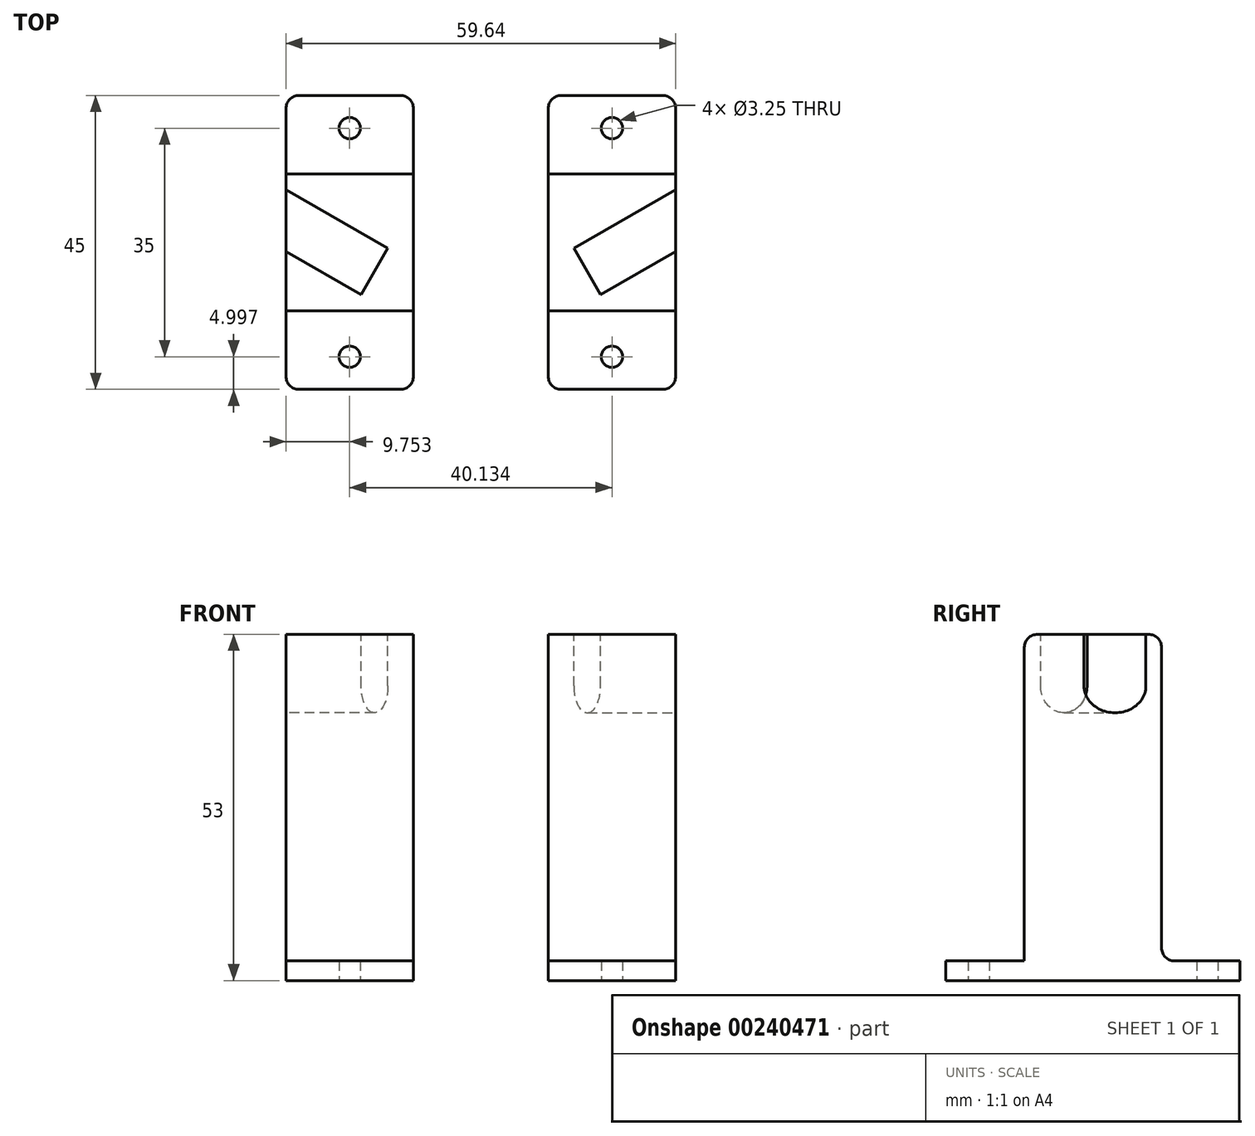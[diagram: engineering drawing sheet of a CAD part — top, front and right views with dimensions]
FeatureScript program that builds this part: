
annotation { "Feature Type Name" : "Feature", "Feature Type Description" : "" }
export const myFeature = defineFeature(function(context is Context, id is Id, definition is map)
    precondition{}
    {
        {
            var Q0;
            Q0=qCreatedBy(makeId("Top.planeOp"),FACE);
            var sketch = newSketch(context, id + "F0", { "sketchPlane" : qUnion([Q0])});
            skLineSegment(sketch, "E0.bottom", {"start": v(-29.82, 23.66) * mm, "end": v(-10.32, 23.66) * mm});
            skLineSegment(sketch, "E0.top", {"start": v(-29.82, -21.34) * mm, "end": v(-10.32, -21.34) * mm});
            skLineSegment(sketch, "E0.left", {"start": v(-29.82, 23.66) * mm, "end": v(-29.82, -21.34) * mm});
            skLineSegment(sketch, "E0.right", {"start": v(-10.32, 23.66) * mm, "end": v(-10.32, -21.34) * mm});
            skPoint(sketch, "E1", {"position": v(-20.07, 18.66) * mm});
            skPoint(sketch, "E1.positionSnap0", {"position": v(-20.07, 23.66) * mm});
            skPoint(sketch, "E2", {"position": v(-20.07, -16.34) * mm});
            skSolve(sketch);
        }
        {
            var Q0;
            Q0=makeQuery(id+"F0.imprint","IMPRINT",FACE,{"disambiguationData":[TD([[makeQuery(id+"F0.imprint","IMPRINT",EDGE,{"derivedFrom":sQuery(id+"F0.wireOp",EDGE,"E0.bottom")}),-1.0]])]});
            extrude(context, id + "F1", {"entities" : qUnion([Q0]), "depth" : 3 * mm});
        }
        {
            var Q0;
            Q0=sQuery(id+"F0.wireOp",VERTEX,"E2");
            var Q1;
            Q1=makeQuery(id+"F1.opExtrude","SWEPT_BODY",BODY,{"disambiguationData":[OSD([sQuery(id+"F0.wireOp",EDGE,"E0.bottom"),sQuery(id+"F0.wireOp",EDGE,"E0.top"),sQuery(id+"F0.wireOp",EDGE,"E0.left"),sQuery(id+"F0.wireOp",EDGE,"E0.right")])]});
            hole(context, id + "F2", {"style" : HoleStyle.SIMPLE, "endStyle" : HoleEndStyle.THROUGH, "oppositeDirection" : true, "holeDiameter" : 3.25 * mm, "locations" : qUnion([Q0]), "scope" : qUnion([Q1]), "isTappedThrough" : true});
        }
        {
            var Q0;
            Q0=sQuery(id+"F0.wireOp",VERTEX,"E1");
            var Q1;
            Q1=makeQuery(id+"F1.opExtrude","SWEPT_BODY",BODY,{"disambiguationData":[OSD([sQuery(id+"F0.wireOp",EDGE,"E0.bottom"),sQuery(id+"F0.wireOp",EDGE,"E0.top"),sQuery(id+"F0.wireOp",EDGE,"E0.left"),sQuery(id+"F0.wireOp",EDGE,"E0.right")])]});
            hole(context, id + "F3", {"style" : HoleStyle.SIMPLE, "endStyle" : HoleEndStyle.THROUGH, "oppositeDirection" : true, "holeDiameter" : 3.25 * mm, "locations" : qUnion([Q0]), "scope" : qUnion([Q1]), "isTappedThrough" : true});
        }
        {
            var Q0;
            Q0=makeQuery(id+"F1.opExtrude","CAP_FACE",FACE,{"disambiguationData":[OSD([sQuery(id+"F0.wireOp",EDGE,"E0.bottom"),sQuery(id+"F0.wireOp",EDGE,"E0.top"),sQuery(id+"F0.wireOp",EDGE,"E0.left"),sQuery(id+"F0.wireOp",EDGE,"E0.right")])],"isStart":false});
            var sketch = newSketch(context, id + "F4", { "sketchPlane" : qUnion([Q0])});
            skLineSegment(sketch, "E3.bottom", {"start": v(-29.82, 11.66) * mm, "end": v(-10.32, 11.66) * mm});
            skLineSegment(sketch, "E3.top", {"start": v(-29.82, -9.34) * mm, "end": v(-10.32, -9.34) * mm});
            skLineSegment(sketch, "E3.left", {"start": v(-29.82, 11.66) * mm, "end": v(-29.82, -9.34) * mm});
            skLineSegment(sketch, "E3.right", {"start": v(-10.32, 11.66) * mm, "end": v(-10.32, -9.34) * mm});
            skSolve(sketch);
        }
        {
            var Q0;
            Q0=makeQuery(id+"F4.imprint","IMPRINT",FACE,{"disambiguationData":[TD([[makeQuery(id+"F4.imprint","IMPRINT",EDGE,{"derivedFrom":sQuery(id+"F4.wireOp",EDGE,"E3.bottom")}),-1.0]])]});
            extrude(context, id + "F5", {"entities" : qUnion([Q0]), "operationType" : NewBodyOperationType.ADD, "depth" : 50 * mm});
        }
        {
            var Q0;
            Q0=makeQuery(id+"F5.opExtrude","CAP_EDGE",EDGE,{"disambiguationData":[OSD([sQuery(id+"F4.wireOp",EDGE,"E3.top")])],"isStart":true});
            var Q1;
            Q1=makeQuery(id+"F5.opExtrude","CAP_EDGE",EDGE,{"disambiguationData":[OSD([sQuery(id+"F4.wireOp",EDGE,"E3.bottom")])],"isStart":true});
            fillet(context, id + "F6", {"entities" : qUnion([Q0, Q1]), "radius" : 2 * mm, "tangentPropagation" : true, "allowEdgeOverflow" : false});
        }
        {
            var Q0;
            Q0=makeQuery(id+"F1.opExtrude","SWEPT_EDGE",EDGE,{"disambiguationData":[OSD([sQuery(id+"F0.wireOp",EDGE,"E0.top"),sQuery(id+"F0.wireOp",EDGE,"E0.right")])]});
            var Q1;
            Q1=makeQuery(id+"F1.opExtrude","SWEPT_EDGE",EDGE,{"disambiguationData":[OSD([sQuery(id+"F0.wireOp",EDGE,"E0.top"),sQuery(id+"F0.wireOp",EDGE,"E0.left")])]});
            var Q2;
            Q2=makeQuery(id+"F1.opExtrude","SWEPT_EDGE",EDGE,{"disambiguationData":[OSD([sQuery(id+"F0.wireOp",EDGE,"E0.bottom"),sQuery(id+"F0.wireOp",EDGE,"E0.right")])]});
            var Q3;
            Q3=makeQuery(id+"F1.opExtrude","SWEPT_EDGE",EDGE,{"disambiguationData":[OSD([sQuery(id+"F0.wireOp",EDGE,"E0.bottom"),sQuery(id+"F0.wireOp",EDGE,"E0.left")])]});
            fillet(context, id + "F7", {"entities" : qUnion([Q0, Q1, Q2, Q3]), "radius" : 2 * mm, "tangentPropagation" : true, "allowEdgeOverflow" : false});
        }
        {
            var Q0;
            Q0=makeQuery(id+"F5.opExtrude","CAP_FACE",FACE,{"disambiguationData":[OSD([sQuery(id+"F4.wireOp",EDGE,"E3.bottom"),sQuery(id+"F4.wireOp",EDGE,"E3.top"),sQuery(id+"F4.wireOp",EDGE,"E3.left"),sQuery(id+"F4.wireOp",EDGE,"E3.right")])],"isStart":false});
            var sketch = newSketch(context, id + "F8", { "sketchPlane" : qUnion([Q0])});
            skLineSegment(sketch, "E4", {"start": v(-29.82, 9.26) * mm, "end": v(-14.23, 0.26) * mm});
            skLineSegment(sketch, "E5", {"start": v(-14.23, 0.26) * mm, "end": v(-18.33, -6.84) * mm});
            skLineSegment(sketch, "E6", {"start": v(-18.33, -6.84) * mm, "end": v(-29.82, -0.2) * mm});
            skSolve(sketch);
        }
        {
            var Q0;
            {var subQ0=sQuery(id+"F8.wireOp",EDGE,"E4");Q0=makeQuery(id+"F8.imprint","IMPRINT",FACE,{"disambiguationData":[TD([[makeQuery(id+"F8.imprint","IMPRINT",EDGE,{"derivedFrom":subQ0}),-1.0]])]});}
            extrude(context, id + "F9", {"entities" : qUnion([Q0]), "operationType" : NewBodyOperationType.REMOVE, "oppositeDirection" : true, "depth" : 12 * mm});
        }
        {
            var Q0;
            Q0=makeQuery(id+"F9.boolean.opBoolean","COPY",EDGE,{"derivedFrom":makeQuery(id+"F9.opExtrude","CAP_EDGE",EDGE,{"disambiguationData":[OSD([sQuery(id+"F8.wireOp",EDGE,"E4")])],"isStart":false})});
            var Q1;
            Q1=makeQuery(id+"F9.boolean.opBoolean","COPY",EDGE,{"derivedFrom":makeQuery(id+"F9.opExtrude","CAP_EDGE",EDGE,{"disambiguationData":[OSD([sQuery(id+"F8.wireOp",EDGE,"E6")])],"isStart":false})});
            fillet(context, id + "F10", {"entities" : qUnion([Q0, Q1]), "radius" : 4.1 * mm, "tangentPropagation" : true, "allowEdgeOverflow" : false});
        }
        {
            var Q0;
            Q0=makeQuery(id+"F5.opExtrude","CAP_EDGE",EDGE,{"disambiguationData":[OSD([sQuery(id+"F4.wireOp",EDGE,"E3.top")])],"isStart":false});
            var Q1;
            Q1=makeQuery(id+"F5.opExtrude","CAP_EDGE",EDGE,{"disambiguationData":[OSD([sQuery(id+"F4.wireOp",EDGE,"E3.bottom")])],"isStart":false});
            fillet(context, id + "F11", {"entities" : qUnion([Q0, Q1]), "radius" : 2 * mm, "tangentPropagation" : true, "allowEdgeOverflow" : false});
        }
        {
            var Q0;
            Q0=makeQuery(id+"F1.opExtrude","SWEPT_BODY",BODY,{"disambiguationData":[OSD([sQuery(id+"F0.wireOp",EDGE,"E0.bottom"),sQuery(id+"F0.wireOp",EDGE,"E0.top"),sQuery(id+"F0.wireOp",EDGE,"E0.left"),sQuery(id+"F0.wireOp",EDGE,"E0.right")])]});
            var Q1;
            Q1=qCreatedBy(makeId("Right.planeOp"),FACE);
            mirror(context, id + "F12", {"entities" : qUnion([Q0]), "mirrorPlane" : qUnion([Q1])});
        }
    });
